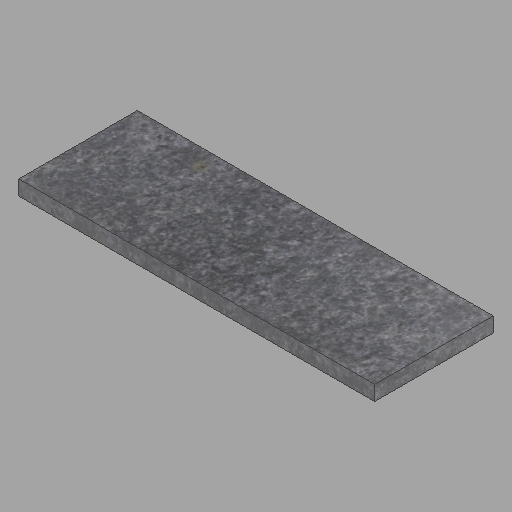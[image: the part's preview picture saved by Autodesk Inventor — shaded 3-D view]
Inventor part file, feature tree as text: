
AUTODESK INVENTOR PART (.ipt)
format: ipt  version: 2023 (Build 270158000, 158)  size: 208,896 bytes
history: native  units: in
note: dims shown in document units (in); Inventor stores cm internally (conversion verified against a paired STEP export)
features: other x1, extrude x1, sketch x1
ambient origin geometry x8: Origin, YZ Plane, XZ Plane, XY Plane, X Axis, Y Axis, Z Axis, Center Point
bodies: Solid1 (feature_tree)
feature tree (3):
  other  "2x16x48-5"
  extrude  "Extrusion1"  Depth=16.0in
  sketch  "Sketch1"  dims[d0=2.0in d1=16.0in d2=48.0in d3=0.0in]
